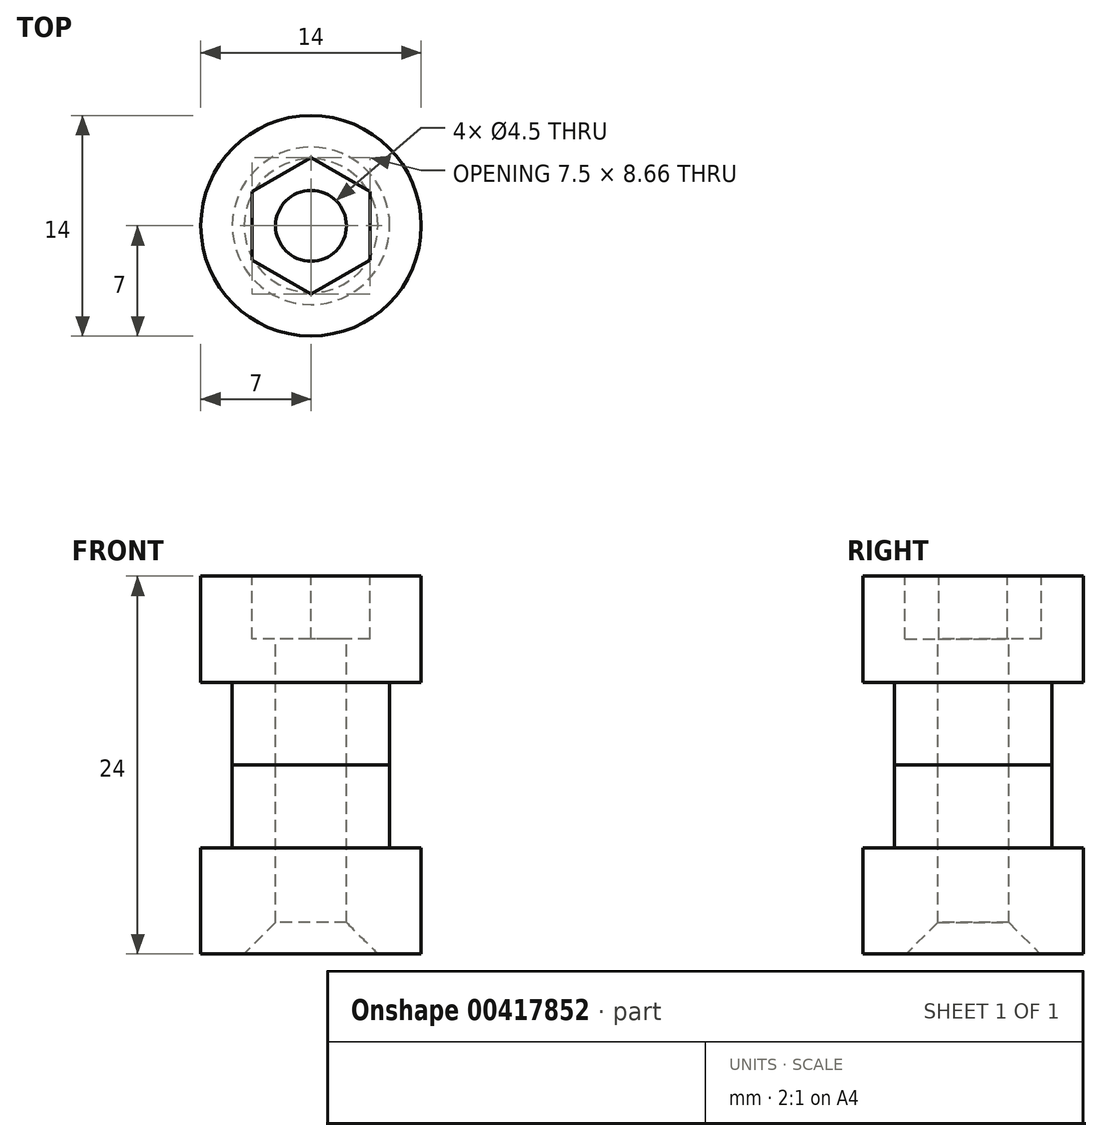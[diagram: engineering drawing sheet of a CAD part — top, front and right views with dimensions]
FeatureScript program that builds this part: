
annotation { "Feature Type Name" : "Feature", "Feature Type Description" : "" }
export const myFeature = defineFeature(function(context is Context, id is Id, definition is map)
    precondition{}
    {
        {
            var Q0;
            Q0=qCreatedBy(makeId("Front.planeOp"),FACE);
            var sketch = newSketch(context, id + "F0", { "sketchPlane" : qUnion([Q0])});
            skLineSegment(sketch, "E0", {"start": v(2.25, 12) * mm, "end": v(2.25, -10) * mm});
            skLineSegment(sketch, "E1", {"start": v(4.25, -12) * mm, "end": v(7, -12) * mm});
            skLineSegment(sketch, "E2", {"start": v(7, -12) * mm, "end": v(7, -5.25) * mm});
            skLineSegment(sketch, "E3", {"start": v(7, -5.25) * mm, "end": v(5, -5.25) * mm});
            skLineSegment(sketch, "E4", {"start": v(5, -5.25) * mm, "end": v(5, 5.25) * mm});
            skLineSegment(sketch, "E5.MirrorCS", {"start": v(2.25, 12) * mm, "end": v(7, 12) * mm});
            skLineSegment(sketch, "E6.MirrorCS", {"start": v(7, 5.25) * mm, "end": v(5, 5.25) * mm});
            skLineSegment(sketch, "E7.MirrorCS", {"start": v(7, 12) * mm, "end": v(7, 5.25) * mm});
            skPoint(sketch, "E8.orphan", {"position": v(7, 12) * mm});
            skLineSegment(sketch, "E9.MirrorCS", {"start": v(-2.25, 12) * mm, "end": v(-2.25, -10) * mm});
            skLineSegment(sketch, "E10.MirrorCS", {"start": v(-2.25, 12) * mm, "end": v(-7, 12) * mm});
            skLineSegment(sketch, "E11.MirrorCS", {"start": v(-7, 12) * mm, "end": v(-7, 5.25) * mm});
            skLineSegment(sketch, "E12.MirrorCS", {"start": v(-7, 5.25) * mm, "end": v(-5, 5.25) * mm});
            skLineSegment(sketch, "E13.MirrorCS", {"start": v(-5, -5.25) * mm, "end": v(-5, 5.25) * mm});
            skLineSegment(sketch, "E14.MirrorCS", {"start": v(-7, -5.25) * mm, "end": v(-5, -5.25) * mm});
            skLineSegment(sketch, "E15.MirrorCS", {"start": v(-4.25, -12) * mm, "end": v(-7, -12) * mm});
            skLineSegment(sketch, "E16.MirrorCS", {"start": v(-7, -12) * mm, "end": v(-7, -5.25) * mm});
            skPoint(sketch, "E17.orphan", {"position": v(5, 5.18) * mm});
            skPoint(sketch, "E18.orphan", {"position": v(-5, 5.18) * mm});
            skLineSegment(sketch, "E19", {"start": v(-5, 0) * mm, "end": v(5, 0) * mm});
            skLineSegment(sketch, "E20", {"start": v(0, 14.35) * mm, "end": v(0, -15.36) * mm, "construction": true});
            skLineSegment(sketch, "E21", {"start": v(-2.25, -10) * mm, "end": v(-4.25, -12) * mm});
            skLineSegment(sketch, "E22.MirrorCS", {"start": v(2.25, -10) * mm, "end": v(4.25, -12) * mm});
            skPoint(sketch, "E23.orphan", {"position": v(2.25, -12) * mm});
            skPoint(sketch, "E24.orphan", {"position": v(-2.25, -12) * mm});
            skSolve(sketch);
        }
        {
            var Q0;
            {var subQ1=sQuery(id+"F0.wireOp",EDGE,"E1");Q0=makeQuery(id+"F0.imprint","IMPRINT",FACE,{"disambiguationData":[TD([[makeQuery(id+"F0.imprint","IMPRINT",EDGE,{"derivedFrom":subQ1}),1.0]])]});}
            var Q1;
            Q1=sQuery(id+"F0.wireOp",EDGE,"E20");
            revolve(context, id + "F1", {"entities" : qUnion([Q0]), "axis" : qUnion([Q1]), "revolveType" : RevolveType.FULL});
        }
        {
            var Q0;
            {var subQ1=sQuery(id+"F0.wireOp",EDGE,"E5.MirrorCS");Q0=makeQuery(id+"F0.imprint","IMPRINT",FACE,{"disambiguationData":[TD([[makeQuery(id+"F0.imprint","IMPRINT",EDGE,{"derivedFrom":subQ1}),-1.0]])]});}
            var Q1;
            Q1=sQuery(id+"F0.wireOp",EDGE,"E20");
            revolve(context, id + "F2", {"entities" : qUnion([Q0]), "axis" : qUnion([Q1]), "revolveType" : RevolveType.FULL});
        }
        {
            var Q0;
            Q0=makeQuery(id+"F2.opRevolve","SWEPT_FACE",FACE,{"disambiguationData":[OSD([sQuery(id+"F0.wireOp",EDGE,"E5.MirrorCS")])]});
            var sketch = newSketch(context, id + "F3", { "sketchPlane" : qUnion([Q0])});
            skCircle(sketch, "E25.cCircle", {"center": v(0, 0) * mm, "radius": 3.75 * mm, "construction": true});
            skLineSegment(sketch, "E25.0", {"start": v(-3.75, -2.17) * mm, "end": v(-3.75, 2.17) * mm});
            skLineSegment(sketch, "E25.1", {"start": v(-3.75, 2.17) * mm, "end": v(0, 4.33) * mm});
            skLineSegment(sketch, "E25.2", {"start": v(0, 4.33) * mm, "end": v(3.75, 2.17) * mm});
            skLineSegment(sketch, "E25.3", {"start": v(3.75, 2.17) * mm, "end": v(3.75, -2.17) * mm});
            skLineSegment(sketch, "E25.4", {"start": v(3.75, -2.17) * mm, "end": v(0, -4.33) * mm});
            skLineSegment(sketch, "E25.5", {"start": v(0, -4.33) * mm, "end": v(-3.75, -2.17) * mm});
            skPoint(sketch, "E25.0.midPoint", {"position": v(-3.75, 0) * mm});
            skSolve(sketch);
        }
        {
            var Q0;
            Q0=makeQuery(id+"F3.imprint","IMPRINT",FACE,{"disambiguationData":[TD([[makeQuery(id+"F3.imprint","IMPRINT",EDGE,{"derivedFrom":sQuery(id+"F3.wireOp",EDGE,"E25.0")}),-1.0]])]});
            extrude(context, id + "F4", {"entities" : qUnion([Q0]), "operationType" : NewBodyOperationType.REMOVE, "oppositeDirection" : true, "depth" : 4 * mm});
        }
    });
